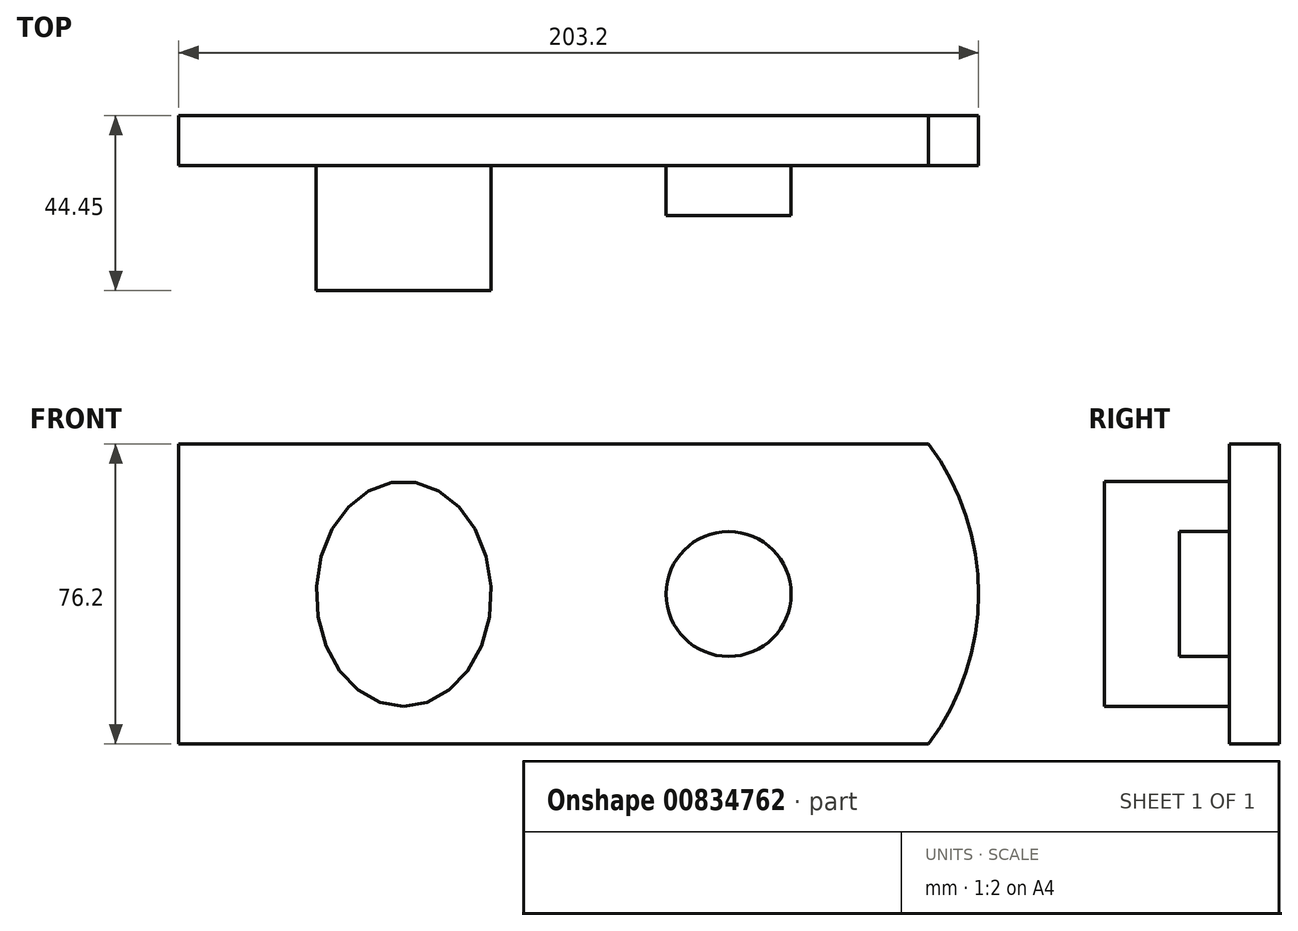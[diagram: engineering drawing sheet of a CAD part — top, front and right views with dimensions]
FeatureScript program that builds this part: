
annotation { "Feature Type Name" : "Feature", "Feature Type Description" : "" }
export const myFeature = defineFeature(function(context is Context, id is Id, definition is map)
    precondition{}
    {
        {
            var Q0;
            Q0=qCreatedBy(makeId("Front.planeOp"),FACE);
            var sketch = newSketch(context, id + "F0", { "sketchPlane" : qUnion([Q0])});
            skLineSegment(sketch, "E0.bottom", {"start": v(95.25, -38.1) * mm, "end": v(-95.25, -38.1) * mm});
            skLineSegment(sketch, "E0.top", {"start": v(95.25, 38.1) * mm, "end": v(-95.25, 38.1) * mm});
            skLineSegment(sketch, "E0.left", {"start": v(95.25, -38.1) * mm, "end": v(95.25, 38.1) * mm});
            skLineSegment(sketch, "E0.right", {"start": v(-95.25, -38.1) * mm, "end": v(-95.25, 38.1) * mm});
            skPoint(sketch, "E0.middle", {"position": v(0, 0) * mm});
            skArc(sketch, "E1", {"start": v(95.25, -38.1) * mm, "mid": v(107.95, 0) * mm, "end": v(95.25, 38.1) * mm});
            skSolve(sketch);
        }
        {
            var Q0;
            Q0 = qSketchRegion(id + "F0", true);
            extrude(context, id + "F1", {"entities" : qUnion([Q0]), "depth" : 12.7 * mm, "offsetDistance" : 25.4 * mm});
        }
        {
            var Q0;
            Q0=makeQuery(id+"F1.opExtrude","CAP_FACE",FACE,{"disambiguationData":[OSD([sQuery(id+"F0.wireOp",EDGE,"E0.bottom"),sQuery(id+"F0.wireOp",EDGE,"E0.top"),sQuery(id+"F0.wireOp",EDGE,"E0.right"),sQuery(id+"F0.wireOp",EDGE,"E1")])],"isStart":false});
            var sketch = newSketch(context, id + "F2", { "sketchPlane" : qUnion([Q0])});
            skEllipse(sketch, "E2", {"center": v(-38.1, 0) * mm, "majorRadius": 28.58 * mm, "minorRadius": 22.23 * mm, "majorAxis": v(0, -1)});
            skSolve(sketch);
        }
        {
            var Q0;
            Q0 = qSketchRegion(id + "F2", true);
            extrude(context, id + "F3", {"entities" : qUnion([Q0]), "operationType" : NewBodyOperationType.ADD, "depth" : 31.75 * mm, "offsetDistance" : 25.4 * mm});
        }
        {
            var Q0;
            Q0=makeQuery(id+"F1.opExtrude","CAP_FACE",FACE,{"disambiguationData":[OSD([sQuery(id+"F0.wireOp",EDGE,"E0.bottom"),sQuery(id+"F0.wireOp",EDGE,"E0.top"),sQuery(id+"F0.wireOp",EDGE,"E0.right"),sQuery(id+"F0.wireOp",EDGE,"E1")])],"isStart":false});
            var sketch = newSketch(context, id + "F4", { "sketchPlane" : qUnion([Q0])});
            skCircle(sketch, "E3", {"center": v(44.45, 0) * mm, "radius": 15.88 * mm});
            skSolve(sketch);
        }
        {
            var Q0;
            Q0 = qSketchRegion(id + "F4", true);
            extrude(context, id + "F5", {"entities" : qUnion([Q0]), "operationType" : NewBodyOperationType.ADD, "depth" : 12.7 * mm, "offsetDistance" : 25.4 * mm});
        }
    });
